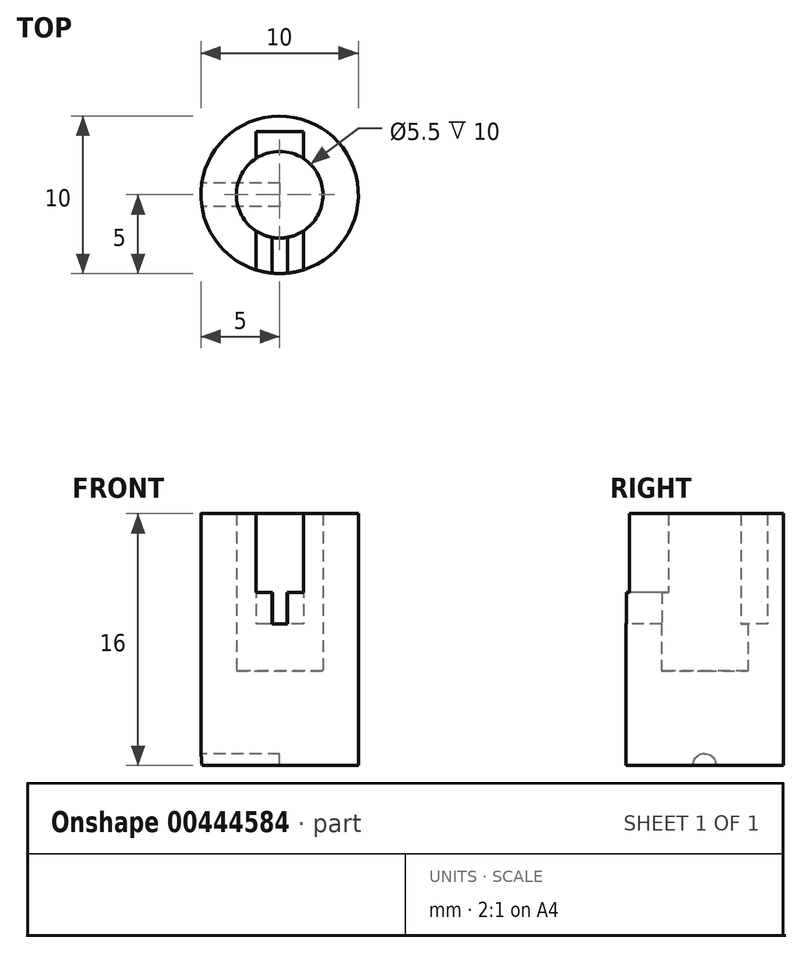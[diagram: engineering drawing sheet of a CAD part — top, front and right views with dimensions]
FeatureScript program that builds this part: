
annotation { "Feature Type Name" : "Feature", "Feature Type Description" : "" }
export const myFeature = defineFeature(function(context is Context, id is Id, definition is map)
    precondition{}
    {
        {
            var Q0;
            Q0=qCreatedBy(makeId("Top.planeOp"),FACE);
            var sketch = newSketch(context, id + "F0", { "sketchPlane" : qUnion([Q0])});
            skCircle(sketch, "E0", {"center": v(0, 0) * mm, "radius": 5 * mm});
            skLineSegment(sketch, "E1.bottom", {"start": v(1.5, 4) * mm, "end": v(-1.5, 4) * mm});
            skLineSegment(sketch, "E1.top", {"start": v(1.5, -5) * mm, "end": v(-1.5, -5) * mm});
            skLineSegment(sketch, "E1.left", {"start": v(1.5, 4) * mm, "end": v(1.5, -5) * mm});
            skLineSegment(sketch, "E1.right", {"start": v(-1.5, 4) * mm, "end": v(-1.5, -5) * mm});
            skLineSegment(sketch, "E2.bottom", {"start": v(-0.5, -2.71) * mm, "end": v(0.5, -2.71) * mm});
            skLineSegment(sketch, "E2.top", {"start": v(-0.5, -5.13) * mm, "end": v(0.5, -5.13) * mm});
            skLineSegment(sketch, "E2.left", {"start": v(-0.5, -2.71) * mm, "end": v(-0.5, -5.13) * mm});
            skLineSegment(sketch, "E2.right", {"start": v(0.5, -2.71) * mm, "end": v(0.5, -5.13) * mm});
            skCircle(sketch, "E3", {"center": v(0, 0) * mm, "radius": 2.75 * mm});
            skSolve(sketch);
        }
        {
            var Q0;
            {var subQ5=sQuery(id+"F0.wireOp",EDGE,"E1.bottom");Q0=makeQuery(id+"F0.imprint","IMPRINT",FACE,{"disambiguationData":[TD([[makeQuery(id+"F0.imprint","IMPRINT",EDGE,{"derivedFrom":subQ5}),-1.0]])]});}
            extrude(context, id + "F1", {"entities" : qUnion([Q0]), "depth" : 5 * mm});
        }
        {
            var Q0;
            {var subQ3=sQuery(id+"F0.wireOp",EDGE,"E0");var subQ5=sQuery(id+"F0.wireOp",EDGE,"E1.left");var subQ6=makeQuery(id+"F0.imprint","INTERSECT",VERTEX,{"derivedFrom":[subQ3,subQ5]});Q0=makeQuery(id+"F0.imprint","IMPRINT",FACE,{"disambiguationData":[TD([[makeQuery(id+"F0.imprint","IMPRINT",EDGE,{"disambiguationData":[TD([[subQ6,1.0]])],"derivedFrom":subQ3}),1.0]])]});}
            var Q1;
            {var subQ3=sQuery(id+"F0.wireOp",EDGE,"E0");var subQ5=sQuery(id+"F0.wireOp",EDGE,"E1.right");var subQ6=makeQuery(id+"F0.imprint","INTERSECT",VERTEX,{"derivedFrom":[subQ3,subQ5]});Q1=makeQuery(id+"F0.imprint","IMPRINT",FACE,{"disambiguationData":[TD([[makeQuery(id+"F0.imprint","IMPRINT",EDGE,{"disambiguationData":[TD([[subQ6,-1.0]])],"derivedFrom":subQ3}),1.0]])]});}
            var Q2;
            Q2=makeQuery(id+"F1.opExtrude","CAP_FACE",FACE,{"disambiguationData":[OSD([sQuery(id+"F0.wireOp",EDGE,"E0"),sQuery(id+"F0.wireOp",EDGE,"E1.bottom"),sQuery(id+"F0.wireOp",EDGE,"E1.left"),sQuery(id+"F0.wireOp",EDGE,"E1.right"),sQuery(id+"F0.wireOp",EDGE,"E3")])],"isStart":false});
            extrude(context, id + "F2", {"entities" : qUnion([Q0, Q1, Q2]), "operationType" : NewBodyOperationType.ADD, "depth" : 2 * mm});
        }
        {
            var Q0;
            Q0=makeQuery(id+"F2.opExtrude","CAP_FACE",FACE,{"disambiguationData":[OSD([sQuery(id+"F0.wireOp",EDGE,"E0"),sQuery(id+"F0.wireOp",EDGE,"E1.bottom"),sQuery(id+"F0.wireOp",EDGE,"E1.left"),sQuery(id+"F0.wireOp",EDGE,"E1.right"),sQuery(id+"F0.wireOp",EDGE,"E3")])],"isStart":false});
            var Q1;
            {var subQ0=sQuery(id+"F0.wireOp",EDGE,"E1.bottom");Q1=makeQuery(id+"F0.imprint","IMPRINT",FACE,{"disambiguationData":[TD([[makeQuery(id+"F0.imprint","IMPRINT",EDGE,{"derivedFrom":subQ0}),1.0]])]});}
            var Q2;
            Q2=makeQuery(id+"F2.opExtrude","CAP_FACE",FACE,{"disambiguationData":[OSD([sQuery(id+"F0.wireOp",EDGE,"E0"),sQuery(id+"F0.wireOp",EDGE,"E1.left"),sQuery(id+"F0.wireOp",EDGE,"E2.bottom"),sQuery(id+"F0.wireOp",EDGE,"E2.right"),sQuery(id+"F0.wireOp",EDGE,"E3")])],"isStart":false});
            var Q3;
            {var subQ6=sQuery(id+"F0.wireOp",EDGE,"E2.left");var subQ8=sQuery(id+"F0.wireOp",EDGE,"E0");var subQ11=makeQuery(id+"F0.imprint","INTERSECT",VERTEX,{"derivedFrom":[subQ8,subQ6]});Q3=makeQuery(id+"F0.imprint","IMPRINT",FACE,{"disambiguationData":[TD([[makeQuery(id+"F0.imprint","IMPRINT",EDGE,{"disambiguationData":[TD([[subQ11,-1.0]])],"derivedFrom":subQ8}),1.0]])]});}
            var Q4;
            Q4=makeQuery(id+"F2.opExtrude","CAP_FACE",FACE,{"disambiguationData":[OSD([sQuery(id+"F0.wireOp",EDGE,"E0"),sQuery(id+"F0.wireOp",EDGE,"E1.right"),sQuery(id+"F0.wireOp",EDGE,"E2.bottom"),sQuery(id+"F0.wireOp",EDGE,"E2.left"),sQuery(id+"F0.wireOp",EDGE,"E3")])],"isStart":false});
            extrude(context, id + "F3", {"entities" : qUnion([Q0, Q1, Q2, Q3, Q4]), "operationType" : NewBodyOperationType.ADD, "depth" : 3 * mm});
        }
        {
            var Q0;
            {var subQ0=sQuery(id+"F0.wireOp",EDGE,"E3");var subQ1=sQuery(id+"F0.wireOp",EDGE,"E1.right");var subQ2=sQuery(id+"F0.wireOp",EDGE,"E1.left");var subQ3=sQuery(id+"F0.wireOp",EDGE,"E1.bottom");var subQ4=sQuery(id+"F0.wireOp",EDGE,"E2.right");var subQ5=sQuery(id+"F0.wireOp",EDGE,"E2.left");var subQ6=sQuery(id+"F0.wireOp",EDGE,"E2.bottom");var subQ7=sQuery(id+"F0.wireOp",EDGE,"E0");Q0=makeQuery(id+"F3.boolean.opBoolean","MERGE",FACE,{"derivedFrom":[makeQuery(id+"F2.boolean.opBoolean","MERGE",FACE,{"derivedFrom":[makeQuery(id+"F1.opExtrude","CAP_FACE",FACE,{"disambiguationData":[OSD([subQ7,subQ3,subQ2,subQ1,subQ0])],"isStart":true}),makeQuery(id+"F2.opExtrude","CAP_FACE",FACE,{"disambiguationData":[OSD([subQ7,subQ1,subQ6,subQ5,subQ0])],"isStart":true}),makeQuery(id+"F2.opExtrude","CAP_FACE",FACE,{"disambiguationData":[OSD([subQ7,subQ2,subQ6,subQ4,subQ0])],"isStart":true})]}),makeQuery(id+"F3.opExtrude","CAP_FACE",FACE,{"disambiguationData":[OSD([subQ7,subQ6,subQ5,subQ4,subQ0])],"isStart":true}),makeQuery(id+"F3.opExtrude","CAP_FACE",FACE,{"disambiguationData":[OSD([subQ3,subQ2,subQ1,subQ0])],"isStart":true})]});}
            var sketch = newSketch(context, id + "F4", { "sketchPlane" : qUnion([Q0])});
            skCircle(sketch, "E4.0", {"center": v(0, 0) * mm, "radius": 2.75 * mm});
            skSolve(sketch);
        }
        {
            var Q0;
            Q0=makeQuery(id+"F4.imprint","IMPRINT",FACE,{"disambiguationData":[TD([[makeQuery(id+"F4.imprint","IMPRINT",EDGE,{"derivedFrom":sQuery(id+"F4.wireOp",EDGE,"E4.0")}),1.0]])]});
            var Q1;
            Q1=makeQuery(id+"F4.imprint","IMPRINT",FACE,{"disambiguationData":[TD([[makeQuery(id+"F4.imprint","IMPRINT",EDGE,{"derivedFrom":sQuery(id+"F4.wireOp",EDGE,"E4.0")}),-1.0]])]});
            extrude(context, id + "F5", {"entities" : qUnion([Q0, Q1]), "operationType" : NewBodyOperationType.ADD, "depth" : 6 * mm});
        }
        {
            var Q0;
            Q0=qCreatedBy(makeId("Right.planeOp"),FACE);
            cPlane(context, id + "F6", {"entities" : qUnion([Q0]), "cplaneType" : CPlaneType.OFFSET, "offset" : 5 * mm, "oppositeDirection" : true, "width" : 150 * mm, "height" : 150 * mm});
        }
        {
            var Q0;
            Q0=qCreatedBy(id+"F6.planeOp",FACE);
            var sketch = newSketch(context, id + "F7", { "sketchPlane" : qUnion([Q0])});
            skLineSegment(sketch, "E5.0", {"start": v(-5, -6) * mm, "end": v(5, -6) * mm});
            skLineSegment(sketch, "E6", {"start": v(-5, -6) * mm, "end": v(-5, 3) * mm});
            skLineSegment(sketch, "E7", {"start": v(5, 10) * mm, "end": v(5, -6) * mm});
            skCircle(sketch, "E8", {"center": v(0, -6) * mm, "radius": 0.75 * mm});
            skSolve(sketch);
        }
        {
            var Q0;
            {var subQ0=sQuery(id+"F7.wireOp",EDGE,"E8");var subQ1=sQuery(id+"F7.wireOp",EDGE,"E5.0");var subQ2=makeQuery(id+"F7.imprint","INTERSECT",VERTEX,{"disambiguationData":[OD(0.0)],"derivedFrom":[subQ1,subQ0]});Q0=makeQuery(id+"F7.imprint","IMPRINT",FACE,{"disambiguationData":[TD([[makeQuery(id+"F7.imprint","IMPRINT",EDGE,{"disambiguationData":[TD([[subQ2,-1.0]])],"derivedFrom":subQ1}),1.0]])]});}
            var Q1;
            {var subQ0=sQuery(id+"F7.wireOp",EDGE,"E8");var subQ1=sQuery(id+"F7.wireOp",EDGE,"E5.0");var subQ2=makeQuery(id+"F7.imprint","INTERSECT",VERTEX,{"disambiguationData":[OD(0.0)],"derivedFrom":[subQ1,subQ0]});Q1=makeQuery(id+"F7.imprint","IMPRINT",FACE,{"disambiguationData":[TD([[makeQuery(id+"F7.imprint","IMPRINT",EDGE,{"disambiguationData":[TD([[subQ2,-1.0]])],"derivedFrom":subQ1}),-1.0]])]});}
            extrude(context, id + "F8", {"entities" : qUnion([Q0, Q1]), "operationType" : NewBodyOperationType.REMOVE, "depth" : 5 * mm});
        }
    });
